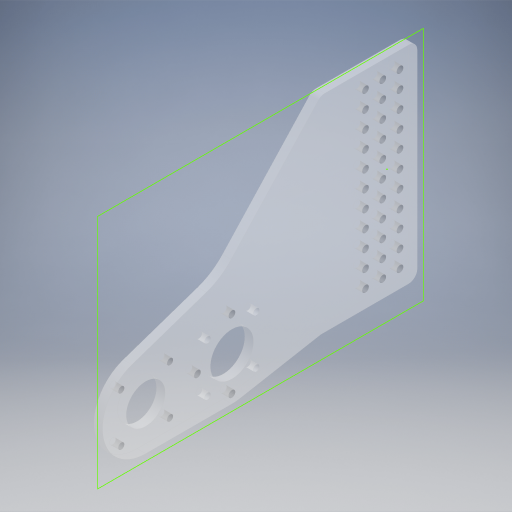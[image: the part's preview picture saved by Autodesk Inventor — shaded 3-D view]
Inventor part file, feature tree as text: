
AUTODESK INVENTOR PART (.ipt)
format: ipt  version: 2024.2 (Build 282272000, 272)  size: 385,536 bytes
history: native  units: in
note: dims shown in document units (in); Inventor stores cm internally (conversion verified against a paired STEP export)
features: sketch x3, projected_geometry x2, other x1, extrude x1
ambient origin geometry x8: Origin, YZ Plane, XZ Plane, XY Plane, X Axis, Y Axis, Z Axis, Center Point
bodies: Solid2 (feature_tree), Solid1 (feature_tree)
feature tree (7):
  other  "Repaired Geometry1"
  sketch  "Sketch1"  dims[d0=1.0in d1=0.0in]
  extrude  "Extrusion1"  [1 undecoded]
  sketch  "Sketch8"
  sketch  "Sketch2"
  projected_geometry  "Projected Loop1"
  projected_geometry  "Projected Loop2"
note: 1 required parameter value undecoded (feature->parameter linkage not recoverable at this tier; creation-order binding heuristic only, values carry confidence <= 0.55)
